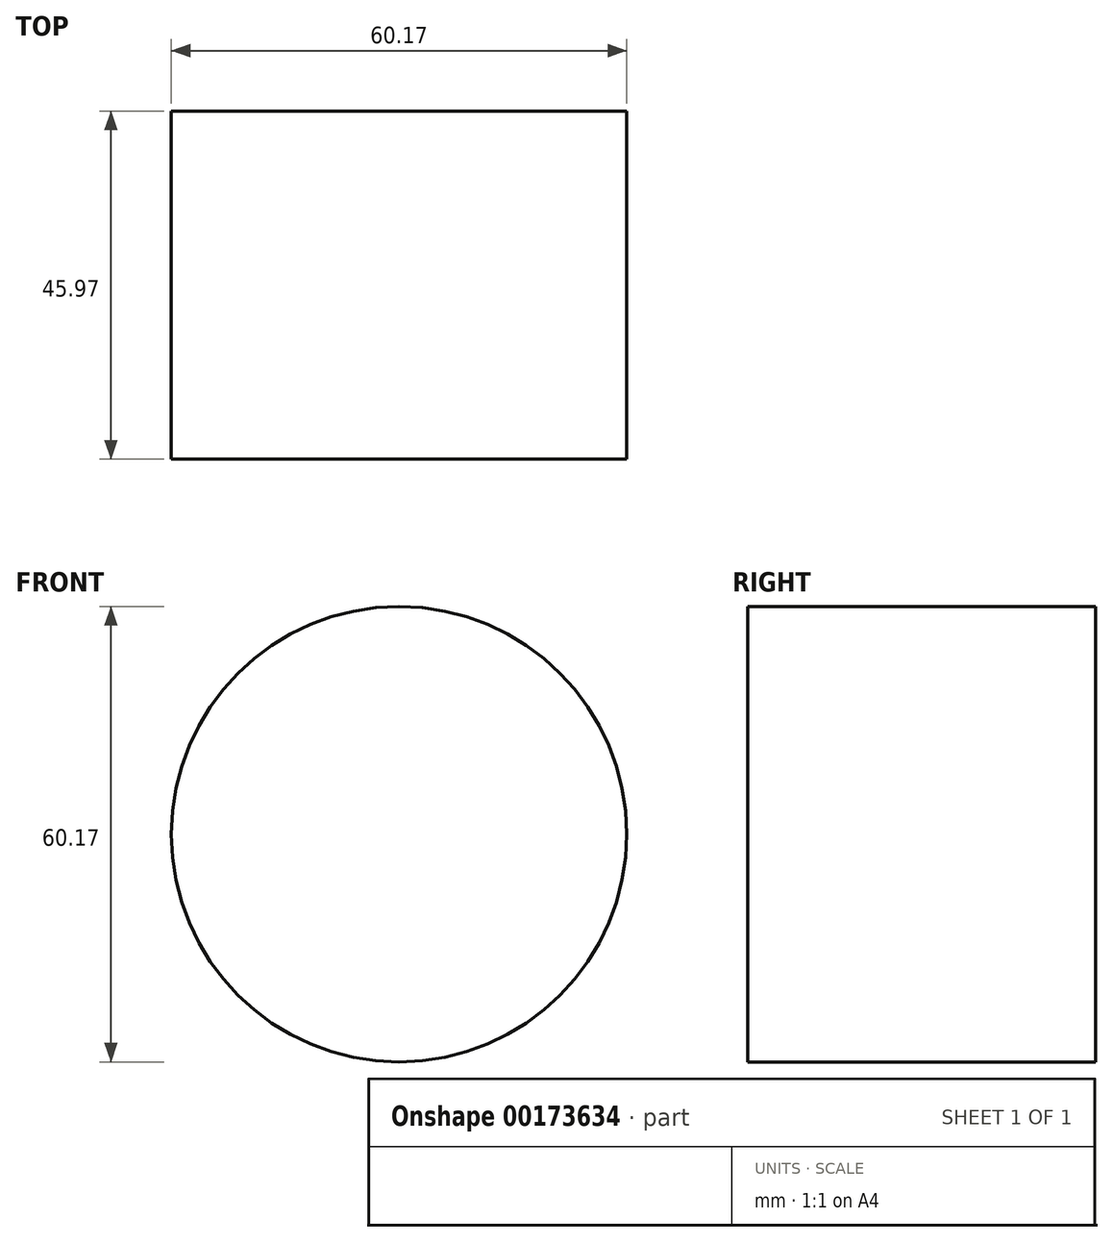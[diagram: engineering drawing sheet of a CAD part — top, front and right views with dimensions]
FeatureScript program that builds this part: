
annotation { "Feature Type Name" : "Feature", "Feature Type Description" : "" }
export const myFeature = defineFeature(function(context is Context, id is Id, definition is map)
    precondition{}
    {
        {
            var Q0;
            Q0=qCreatedBy(makeId("Front.planeOp"),FACE);
            var sketch = newSketch(context, id + "F0", { "sketchPlane" : qUnion([Q0])});
            skCircle(sketch, "E0", {"center": v(-8.43, 17.88) * mm, "radius": 30.08 * mm});
            skSolve(sketch);
        }
        {
            var Q0;
            Q0=makeQuery(id+"F0.imprint","IMPRINT",FACE,{"disambiguationData":[TD([[makeQuery(id+"F0.imprint","IMPRINT",EDGE,{"derivedFrom":sQuery(id+"F0.wireOp",EDGE,"E0")}),1.0]])]});
            extrude(context, id + "F1", {"entities" : qUnion([Q0]), "depth" : 45.97 * mm});
        }
    });
